# Revit family: IS_LDV_T5505_BIM_NL
name_source: partatom
category: Plumbing Fixtures
units: mm (PartAtom-declared; Revit-internal decimal feet)

## family parameters
Always vertical = No
Cut with Voids When Loaded = No
OmniClass Number = 23.45.05.14.21.11
OmniClass Title = Bath/Shower Units
Part Type = Normal
Room Calculation Point = No
Round Connector Dimension = Use Diameter
Shared = No
Work Plane-Based = No

## types (4) — shared parameters
Accessories = http://www.idealstandard.nl
Afmetingen = 60 x 470 x 85 mm
AfstandsEenheid = Millimeter
AreaUnits = millimetres
AssetType = Fixed
Auteur = Ideal Standard
BIMObjectName = IS_IdealStandard_SanitaryAccessories_DolceVita_T5505
BIMobject category = Sanitary: Toilet Accssories
BIMobject main category = Sanitary
BIMobject main category code = Sanitary
Beschrijvinggarantie = Herstellergarantie
Bestanddelen = http://www.idealstandard.nl
BimObjectNaam = IS_IdealStandard_SanitaryAccessories_DolceVita_T5505
Brand = Ideal Standard
Brand url = http://www.idealstandard.nl
Breedte = 60.22867
Category = Plumbing
Classification = Sanitary
ConnectionType = Plumbing
CurrencyUnit = €
CurrentRevision = 1
Date of publishing = 24/01/2023
Diepte = 469 mm
DurationUnit = Years
DuurEenheid = Jahr
Edition number = 1
ElementType = Sanitary Accessories
Garantieunits = Jahre
GemaaktOp = 24/01/2023
Help = http://www.idealstandard.nl
Hoogte = 84.804515838623
IFC Classification = Sanitary Terminal
IfcExportAs = IfcFurnitureType
IfcExportType = TOWELRAIL
Installatieinstructies = http://www.idealstandard.nl
Installation instructions = http://www.idealstandard.nl
InstallationInstructions = http://www.idealstandard.nl
Lengte = 469 mm
LinearUnits = millimeters
MaintenanceInformation = http://www.idealstandard.nl
Manufacturer = Ideal Standard
Manufacturer name = Ideal Standard
ManufacturerURL = http://www.idealstandard.nl
Materiaal = Messing&Stahl
Material = brass&steel
Material main = brass&steel
Merk = Ideal Standard
NBS Reference Code = 45-35-72/372
NBS Reference Description = Towel rails
Name = SanitaryAccessories_DolceVita_T5505_IdealStandard
NettWeight = 0
NominalDepth = 469 mm
NominalHeight = 85 mm
NominalLength = 469 mm
NominalWidth = 60 mm
OppervlakteAfmeting = Millimeter
OppervlakteEenheid = Millimeter
PredefinedType = Sanitary Accessories
Product Guid = 8e0b35c3-107c-4500-871b-7aacebd71822
Product SKU = T5505
Product certification = http://www.idealstandard.nl
Product data url = https://bimobject.com
Product family = Dolce Vita
Product group = Accessories
Product name = Dolce Vita Towel bar vertical double
Product url = http://www.idealstandard.nl
ProductInformation = http://www.idealstandard.nl
Productinformatie = http://www.idealstandard.nl
QR code = http://bimobject.com
Revisie = 1
Shape = cilindrical
Size = 60 x 470 x 85 mm
Space = Internal
SpareParts = http://www.idealstandard.nl
Technical description = http://www.idealstandard.nl
Telefoonnummer = 077 355 08 08
Typeconnectie = Installation
UNSPSC Code = 30181500
URL = http://www.idealstandard.nl
Uniclass 1.4 Code = N14
Uniclass 1.4 Description = Accessories
Uniclass 2015 Code = Pr_40_20_76
Uniclass 2015 Name = Sanitary accessories
Uniclass2015Beschrijving = Sanitary accessories
Uniclass2015Code = Pr_40_20_76
Uniclass2015Referentie = Sanitary accessories
Uniclass2015Title = Sanitary accessories
Uniclass2015Version = V1.26
Uniformat II Code = C1030
Uniformat II Description = Fittings
Urlproducent = http://www.idealstandard.nl
ValutaEenheid = €
Versie = 1
Version = 1
VolumeUnits = Liters
Volumeunits = Liter
Vorm = Zylinder
WRASURL = https://www.wrasapprovals.co.uk
WarrantyDescription = Manufacturers Warranty
WarrantyDurationUnit = Years
Wisselstukken = http://www.idealstandard.nl
Youtube clip = https://www.youtube.com
zero-valued in all types: BrutoGewicht, Cost, Nettogewicht, Vervangingskosten, Weight Net (Kg)

## per-type parameters (varying)
| type | Afwerking | Artikelnummer | Artikelomschrijving | BarCode | Color | Description | Features | Finish | GTIN code | Kleur | MainColor | Model | ModelNumber | ModelReference |
| T5505AA - Dolce Vita Towel bar vertical double  - Chrome | Chrom | T5505AA | Dolce Vita Handtuchhalter vertikal doppelt - Chrom | 8014140514268 | Chrome | Dolce Vita Towel bar vertical double - Chrome | Towel bar vertical double - Chrome | Chrome | 8014140514268 | Chrom | Chrome | T5505AA | T5505AA | Dolce Vita Towel bar vertical double |
| T5505A2 - Dolce Vita Towel bar  vertical double - Brushed gold | Gebürstetes Gold | T5505A2 | Dolce Vita Handtuchhalter vertikal doppelt - Gebürstetes Gold | 8014140514244 | Brushed gold | Dolce Vita Towel bar  vertical double - Brushed gold | Towel bar  vertical double - Brushed gold | Brushed gold | 8014140514244 | Gebürstetes Gold | Brushed gold | T5505A2 | T5505A2 | Dolce Vita Towel bar  vertical double |
| T5505A5 - Dolce Vita Towel bar vertical double - Magnetic grey | Magnetisch grau | T5505A5 | Dolce Vita Handtuchhalter vertikal doppelt - Magnetisch grau | 8014140514251 | Magnetic grey | Dolce Vita Towel bar vertical double - Magnetic grey | Towel bar vertical double - Magnetic grey | Magnetic grey | 8014140514251 | Magnetisch grau | Magnetic grey | T5505A5 | T5505A5 | Dolce Vita Towel bar vertical double |
| T5505GN - Dolce Vita Towel bar vertical double - Silver storm | Silbersturm | T5505GN | Dolce Vita Handtuchhalter vertikal doppelt - Silver Storm | 8014140514275 | Silver storm | Dolce Vita Towel bar vertical double - Silver storm | Towel bar vertical double - Silver storm | Silver storm | 8014140514275 | Silbersturm | Silver storm | T5505GN | T5505GN | Dolce Vita Towel bar vertical double |

## geometry (parser evidence)
native form markers: Sweep x4
no freeform markers — native parametric forms only
